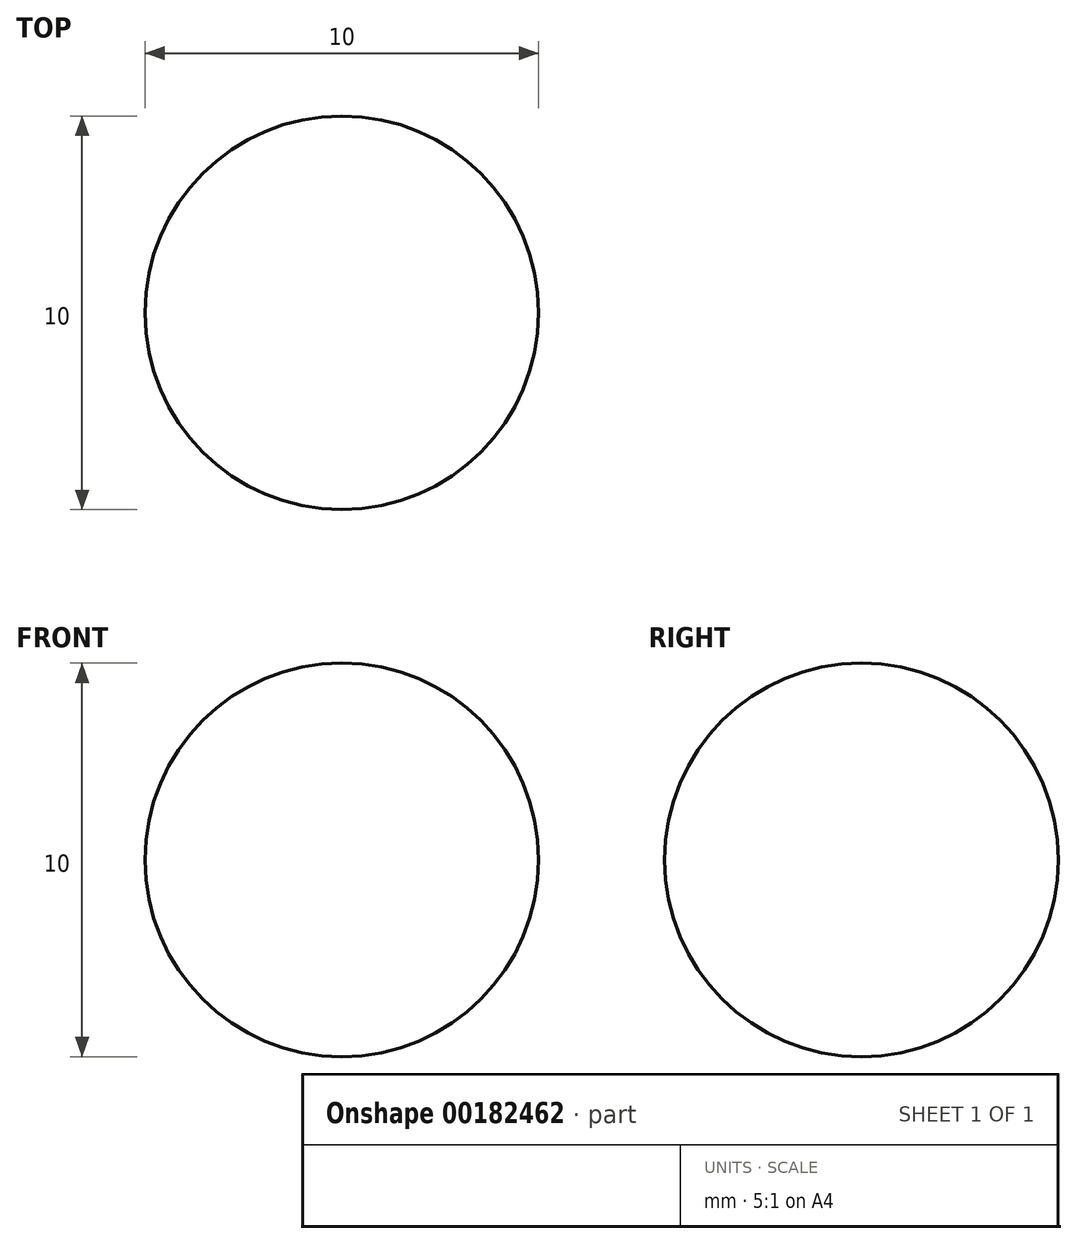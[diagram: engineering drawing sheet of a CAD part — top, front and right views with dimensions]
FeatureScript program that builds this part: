
annotation { "Feature Type Name" : "Feature", "Feature Type Description" : "" }
export const myFeature = defineFeature(function(context is Context, id is Id, definition is map)
    precondition{}
    {
        {
            var Q0;
            Q0=qCreatedBy(makeId("Top.planeOp"),FACE);
            var sketch = newSketch(context, id + "F0", { "sketchPlane" : qUnion([Q0])});
            skLineSegment(sketch, "E0", {"start": v(0, 0) * mm, "end": v(0, 10) * mm});
            skArc(sketch, "E1", {"start": v(0, 0) * mm, "mid": v(5, 5) * mm, "end": v(0, 10) * mm});
            skSolve(sketch);
        }
        {
            var Q0;
            Q0=makeQuery(id+"F0.imprint","IMPRINT",FACE,{"disambiguationData":[TD([[makeQuery(id+"F0.imprint","IMPRINT",EDGE,{"derivedFrom":sQuery(id+"F0.wireOp",EDGE,"E0")}),-1.0]])]});
            var Q1;
            Q1=sQuery(id+"F0.wireOp",EDGE,"E0");
            revolve(context, id + "F1", {"entities" : qUnion([Q0]), "axis" : qUnion([Q1]), "revolveType" : RevolveType.FULL});
        }
    });
